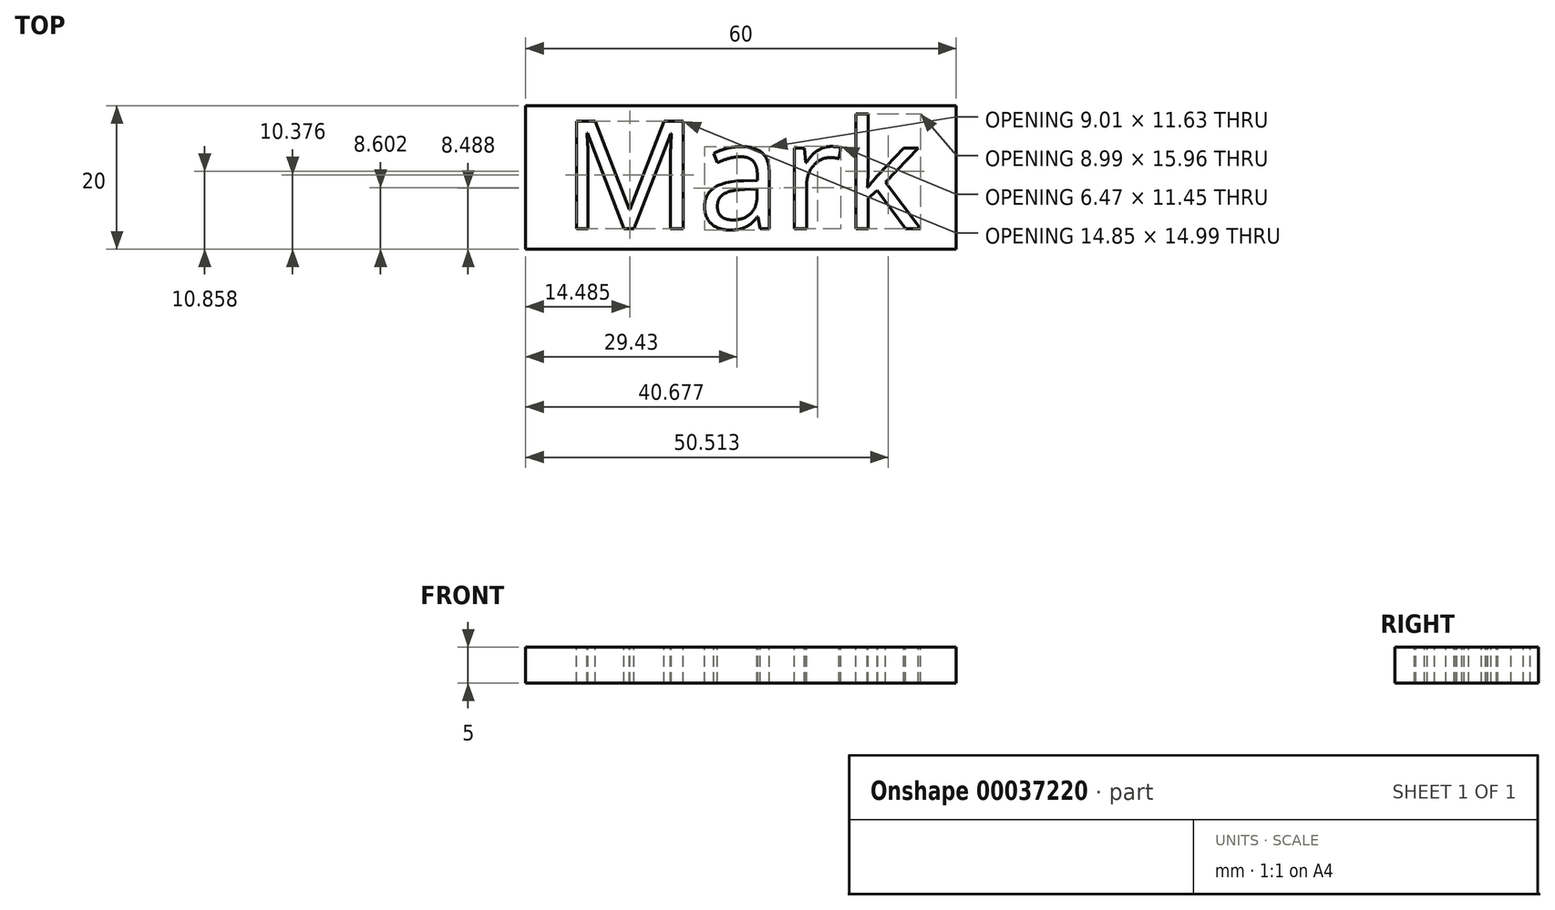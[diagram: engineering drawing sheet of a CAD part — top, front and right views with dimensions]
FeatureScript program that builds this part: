
annotation { "Feature Type Name" : "Feature", "Feature Type Description" : "" }
export const myFeature = defineFeature(function(context is Context, id is Id, definition is map)
    precondition{}
    {
        {
            var Q0;
            Q0=qCreatedBy(makeId("Top.planeOp"),FACE);
            var sketch = newSketch(context, id + "F0", { "sketchPlane" : qUnion([Q0])});
            skLineSegment(sketch, "E0.rect.bottom", {"start": v(30, -10) * mm, "end": v(-30, -10) * mm});
            skLineSegment(sketch, "E0.rect.top", {"start": v(30, 10) * mm, "end": v(-30, 10) * mm});
            skLineSegment(sketch, "E0.rect.left", {"start": v(30, -10) * mm, "end": v(30, 10) * mm});
            skLineSegment(sketch, "E0.rect.right", {"start": v(-30, -10) * mm, "end": v(-30, 10) * mm});
            skPoint(sketch, "E0.rect.middle", {"position": v(0, 0) * mm});
            skSolve(sketch);
        }
        {
            var Q0;
            Q0 = qSketchRegion(id + "F0", true);
            extrude(context, id + "F1", {"entities" : qUnion([Q0]), "depth" : 5 * mm});
        }
        {
            var Q0;
            Q0=makeQuery(id+"F1.opExtrude","CAP_FACE",FACE,{"disambiguationData":[OSD([sQuery(id+"F0.wireOp",EDGE,"E0.rect.bottom"),sQuery(id+"F0.wireOp",EDGE,"E0.rect.top"),sQuery(id+"F0.wireOp",EDGE,"E0.rect.left"),sQuery(id+"F0.wireOp",EDGE,"E0.rect.right")])],"isStart":false});
            var sketch = newSketch(context, id + "F2", { "sketchPlane" : qUnion([Q0])});
            skText(sketch, "E1", { "text": "Mark\n", "fontName": "OpenSans-Regular.ttf"});
            const initialGuessF2  = {"E1": [-0.025, -0.00712, 1, 0, 0.01512]};
            skSetInitialGuess(sketch, initialGuessF2);
            skSolve(sketch);
        }
        {
            var Q0;
            Q0 = qSketchRegion(id + "F2", true);
            extrude(context, id + "F3", {"entities" : qUnion([Q0]), "operationType" : NewBodyOperationType.REMOVE, "endBound" : BoundingType.THROUGH_ALL, "oppositeDirection" : true, "depth" : 25 * mm});
        }
    });
